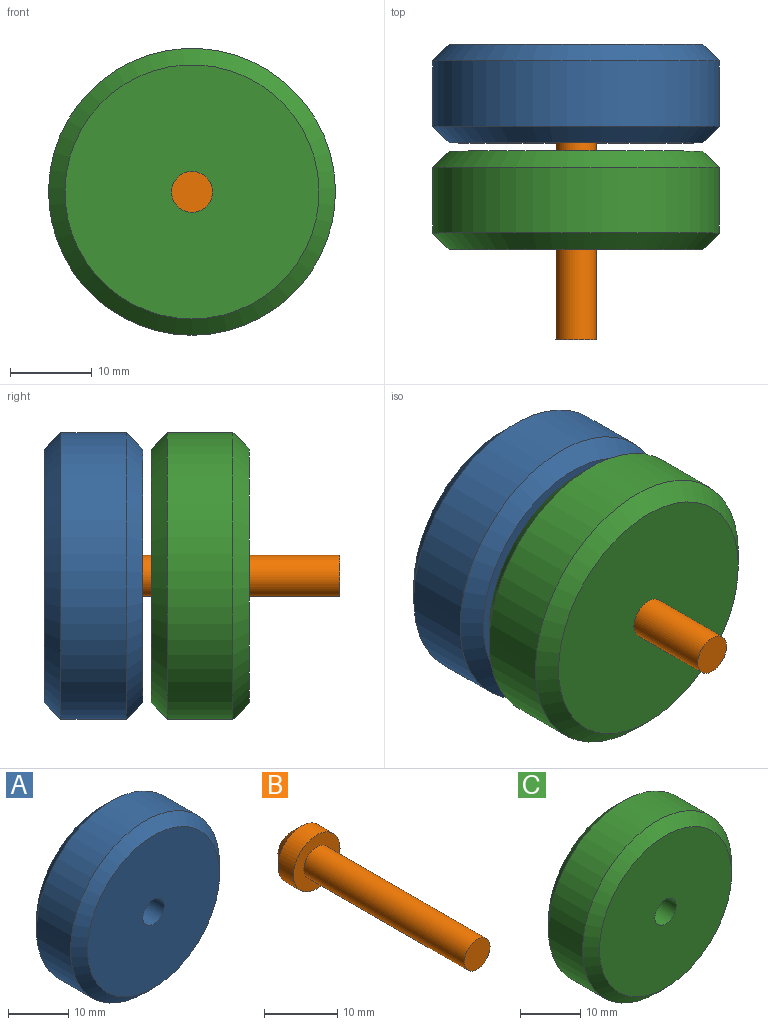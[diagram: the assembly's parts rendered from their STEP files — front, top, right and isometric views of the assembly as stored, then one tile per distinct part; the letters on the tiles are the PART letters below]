
ASSEMBLY  parts=3 mates=4
PART A: 9 faces, bbox 35x12x35 mm
  f0: cylinder r=17.5mm len=35mm, axis (0,1,0), area 879.6mm2, adj f7,f8
  f1: cylinder r=2.5mm len=7mm, axis (0,1,0), area 110mm2, adj f2,f5
  f2: plane 31x31mm, normal (0,-1,0), area 735.1mm2, adj f1,f7
  f3: plane 31x31mm, normal (0,1,0), area 391.7mm2, adj f6,f8
  f4: cylinder r=8.75mm len=17.5mm, axis (0,1,0), area 164.9mm2, adj f5,f6
  f5: plane 17.5x17.5mm, normal (0,1,0), area 220.9mm2, adj f1,f4
  f6: cone r=10.75mm half-angle=45deg, axis (0,1,0), area 173.3mm2, adj f3,f4
  f7: cone r=15.5mm half-angle=45deg, axis (0,1,0), area 293.2mm2, adj f0,f2
  f8: cone r=17.5mm half-angle=45deg, axis (0,-1,0), area 293.2mm2, adj f0,f3
PART B: 6 faces, bbox 9x36x9 mm
  f0: cylinder r=2.5mm len=31mm, axis (0,1,0), area 486.9mm2, adj f1,f3
  f1: plane 5x5mm, normal (0,-1,0), area 19.6mm2, adj f0
  f2: cylinder r=4.5mm len=9mm, axis (0,1,0), area 84.8mm2, adj f3,f5
  f3: plane 9x9mm, normal (0,-1,0), area 44mm2, adj f0,f2
  f4: plane 5x5mm, normal (0,1,0), area 19.6mm2, adj f5
  f5: cone r=4.5mm half-angle=45deg, axis (0,-1,0), area 62.2mm2, adj f2,f4
PART C: 6 faces, bbox 35x12x35 mm
  f0: cylinder r=17.5mm len=35mm, axis (0,1,0), area 879.6mm2, adj f4,f5
  f1: cylinder r=2.5mm len=12mm, axis (0,1,0), area 188.5mm2, adj f2,f3
  f2: plane 31x31mm, normal (0,-1,0), area 735.1mm2, adj f1,f4
  f3: plane 31x31mm, normal (0,1,0), area 735.1mm2, adj f1,f5
  f4: cone r=15.5mm half-angle=45deg, axis (0,1,0), area 293.2mm2, adj f0,f2
  f5: cone r=17.5mm half-angle=45deg, axis (0,-1,0), area 293.2mm2, adj f0,f3
PLACE A t=(-55.18,61.95,2.54)mm
PLACE B t=(-55.18,61.95,2.54)mm
PLACE C t=(-55.18,61.45,2.54)mm
MATE planar C.f0 <-> A.f0  axis (0,1,0) through (27.82,48.95,2.54)mm
MATE planar A.f0 <-> B.f0  axis (0,1,0) through (27.82,56.95,2.54)mm
MATE slider C.f0 <-> B.f0  axis (0,1,0) through (27.82,42.95,2.54)mm
MATE cylindrical A.f0 <-> B.f0  axis (0,1,0) through (27.82,53.45,2.54)mm
